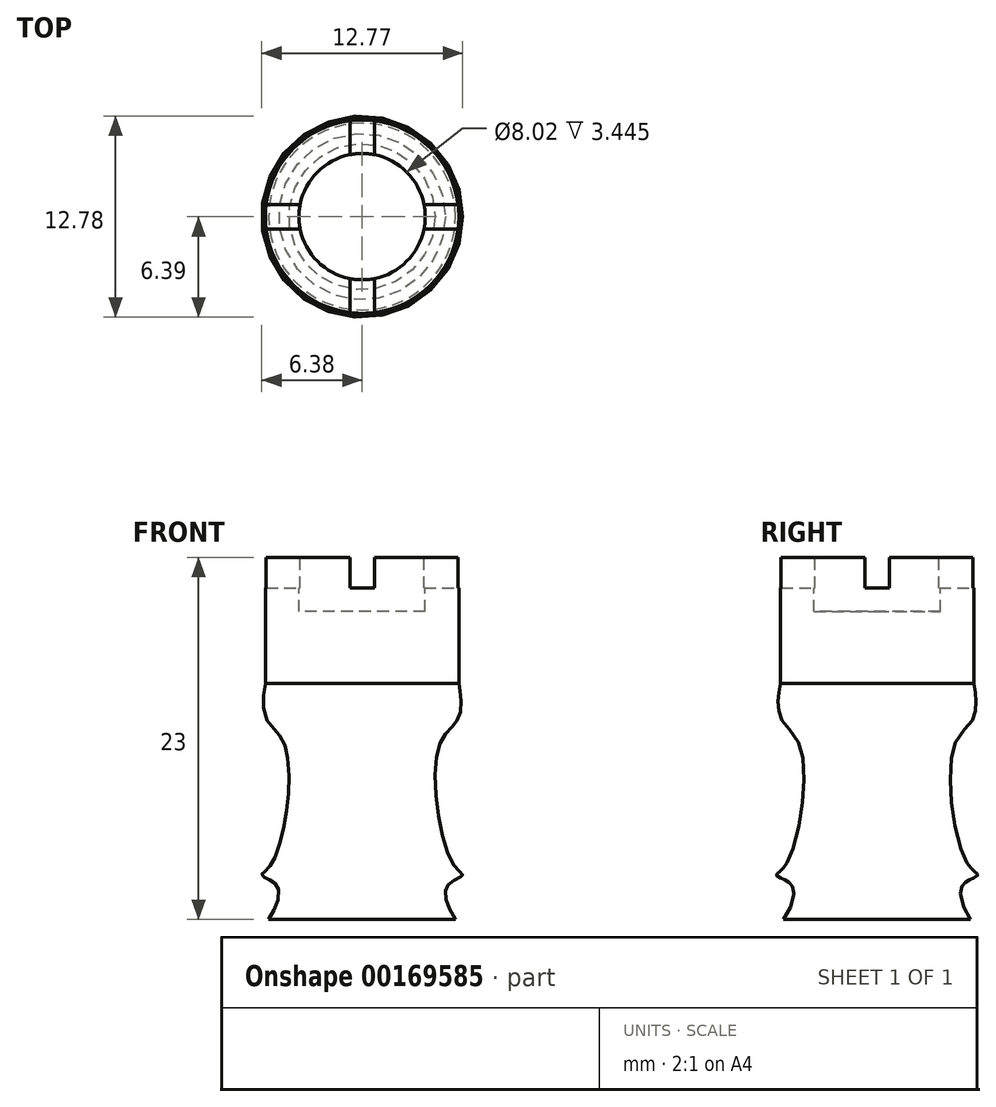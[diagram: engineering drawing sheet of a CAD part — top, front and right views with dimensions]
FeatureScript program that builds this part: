
annotation { "Feature Type Name" : "Feature", "Feature Type Description" : "" }
export const myFeature = defineFeature(function(context is Context, id is Id, definition is map)
    precondition{}
    {
        {
            var Q0;
            Q0=qCreatedBy(makeId("Front.planeOp"),FACE);
            var sketch = newSketch(context, id + "F0", { "sketchPlane" : qUnion([Q0])});
            skLineSegment(sketch, "E0.bottom", {"start": v(-4.01, 46.3) * mm, "end": v(-6.15, 46.3) * mm});
            skLineSegment(sketch, "E0.top", {"start": v(0, 38.3) * mm, "end": v(-6.15, 38.3) * mm});
            skLineSegment(sketch, "E0.left", {"start": v(0, 42.86) * mm, "end": v(0, 38.3) * mm});
            skLineSegment(sketch, "E0.right", {"start": v(-6.15, 46.3) * mm, "end": v(-6.15, 38.3) * mm});
            skLineSegment(sketch, "E1.top", {"start": v(-4.01, 42.86) * mm, "end": v(0, 42.86) * mm});
            skLineSegment(sketch, "E1.left", {"start": v(-4.01, 46.3) * mm, "end": v(-4.01, 42.86) * mm});
            skPoint(sketch, "E2.orphan", {"position": v(0, 46.3) * mm});
            skFitSpline(sketch, "E3", {"points": [v(-6.15, 38.3) * mm, v(-6.15, 36.16) * mm, v(-4.88, 34.3) * mm, v(-5.79, 26.78) * mm, v(-6.38, 26.1) * mm, v(-5.54, 25.6) * mm, v(-5.45, 24.24) * mm, v(-7.23, 21.1) * mm, v(-7.48, 19.59) * mm, v(-7.14, 18.15) * mm, v(-6.3, 17.73) * mm, v(-6.97, 16.71) * mm, v(-9, 14.3) * mm, v(0, 13.22) * mm], "startDerivative": vector(-4, -17.38) * mm, "endDerivative": vector(48.53, 7.54) * mm});
            skLineSegment(sketch, "E4", {"start": v(0, 14.2) * mm, "end": v(0, 13.22) * mm});
            skPoint(sketch, "E5.orphan", {"position": v(216.1, 13.22) * mm});
            skLineSegment(sketch, "E6", {"start": v(0, 23.3) * mm, "end": v(0, 42.86) * mm});
            skLineSegment(sketch, "E7", {"start": v(-5.93, 23.3) * mm, "end": v(0, 23.3) * mm});
            skPoint(sketch, "E8.orphan", {"position": v(13.85, 23.3) * mm});
            skPoint(sketch, "E9.orphan", {"position": v(0, 26.52) * mm});
            skSolve(sketch);
        }
        {
            var Q0;
            Q0=qCreatedBy(makeId("Front.planeOp"),FACE);
            var sketch = newSketch(context, id + "F1", { "sketchPlane" : qUnion([Q0])});
            skLineSegment(sketch, "E10", {"start": v(0, 42.86) * mm, "end": v(0, 13.5) * mm});
            skSolve(sketch);
        }
        {
            var Q0;
            Q0 = qSketchRegion(id + "F0", true);
            var Q1;
            Q1=sQuery(id+"F1.wireOp",EDGE,"E10");
            revolve(context, id + "F2", {"entities" : qUnion([Q0]), "axis" : qUnion([Q1]), "revolveType" : RevolveType.FULL});
        }
        {
            var Q0;
            Q0=qCreatedBy(makeId("Front.planeOp"),FACE);
            var sketch = newSketch(context, id + "F3", { "sketchPlane" : qUnion([Q0])});
            skLineSegment(sketch, "E11.bottom", {"start": v(0, 46.31) * mm, "end": v(-0.78, 46.31) * mm});
            skLineSegment(sketch, "E11.top", {"start": v(0.35, 44.35) * mm, "end": v(-0.78, 44.35) * mm});
            skLineSegment(sketch, "E11.right", {"start": v(-0.78, 46.31) * mm, "end": v(-0.78, 44.35) * mm});
            skLineSegment(sketch, "E12.MirrorCS", {"start": v(-0.35, 44.35) * mm, "end": v(0.78, 44.35) * mm});
            skLineSegment(sketch, "E13.MirrorCS", {"start": v(0.78, 46.31) * mm, "end": v(0.78, 44.35) * mm});
            skLineSegment(sketch, "E14.MirrorCS", {"start": v(0, 46.31) * mm, "end": v(0.78, 46.31) * mm});
            skSolve(sketch);
        }
        {
            var Q0;
            Q0 = qSketchRegion(id + "F3", true);
            extrude(context, id + "F4", {"entities" : qUnion([Q0]), "depth" : 25 * mm, "symmetric" : true});
        }
        {
            var Q0;
            Q0=qCreatedBy(makeId("Front.planeOp"),FACE);
            var sketch = newSketch(context, id + "F5", { "sketchPlane" : qUnion([Q0])});
            skLineSegment(sketch, "E15", {"start": v(0, 50.19) * mm, "end": v(0, 0) * mm});
            skSolve(sketch);
        }
        {
            var Q0;
            Q0=makeQuery(id+"F4.opExtrude","SWEPT_BODY",BODY,{"disambiguationData":[OSD([sQuery(id+"F3.wireOp",EDGE,"E11.bottom"),sQuery(id+"F3.wireOp",EDGE,"E11.top"),sQuery(id+"F3.wireOp",EDGE,"E11.right"),sQuery(id+"F3.wireOp",EDGE,"E12.MirrorCS"),sQuery(id+"F3.wireOp",EDGE,"E13.MirrorCS"),sQuery(id+"F3.wireOp",EDGE,"E14.MirrorCS")])]});
            var Q1;
            Q1=sQuery(id+"F5.wireOp",EDGE,"E15");
            circularPattern(context, id + "F6", {"operationType" : NewBodyOperationType.REMOVE, "entities" : qUnion([Q0]), "axis" : qUnion([Q1]), "angle" : 90 * degree, "instanceCount" : 2, "computeTransformsWithoutBuiltin" : true});
        }
    });
